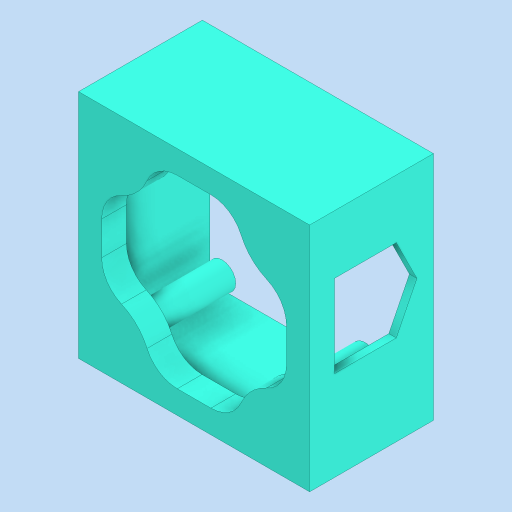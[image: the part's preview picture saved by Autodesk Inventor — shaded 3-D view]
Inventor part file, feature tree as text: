
AUTODESK INVENTOR PART (.ipt)
format: ipt  version: 2024 (Build 280153000, 153)  size: 608,768 bytes
history: native  units: in
note: dims shown in document units (in); Inventor stores cm internally (conversion verified against a paired STEP export)
features: extrude x8, sketch x7, plane x1
ambient origin geometry x8: Origin, YZ Plane, XZ Plane, XY Plane, X Axis, Y Axis, Z Axis, Center Point
bodies: Solid1 (feature_tree)
feature tree (16):
  extrude  "Base"  Depth=0.14in
  extrude  "Open Back"  Depth=0.15in TaperAngle=0.0deg
  extrude  "Housing"  Depth=0.453in TaperAngle=0.0deg
  plane  "Work Plane1"
  extrude  "HoleClosing"  Depth=0.09in
  extrude  "Cable Hole"  Depth=0.045in
  extrude  "Pegs"  Depth=0.045in
  extrude  "Zip-Tie Attachment"  Depth=0.045in TaperAngle=0.0deg
  extrude  "top left hole"  Depth=0.045in
  sketch  "Sketch1"  dims[d9=0.15in d10=0.0in d13=0.14in]
  sketch  "Sketch2"  dims[d16=0.14in d18=0.15in d19=0.0in]
  sketch  "Sketch3"  dims[d21=0.0369in d24=0.453in d25=0.0in]
  sketch  "Sketch10"  dims[d26=0.09in d30=0.09in]
  sketch  "Sketch15"  dims[d31=0.037in d32=0.045in]
  sketch  "Sketch16"  dims[d33=0.045in d34=0.045in]
  sketch  "Sketch17"  dims[d35=0.045in d36=0.6in d37=0.0in d38=1.2598in d49=0.0in d84=0.05in d85=0.0in d101=1.12in d102=0.3in d103=0.3in d104=0.3in d105=0.3in d106=0.2in d107=0.35in d108=0.56in d110=0.15in d111=0.0in d116=0.866in d117=0.164in d118=0.222in d119=0.0in d120=0.453in d121=0.0in d52=0.5in d53=0.0344in d54=0.5in d55=0.0344in]
